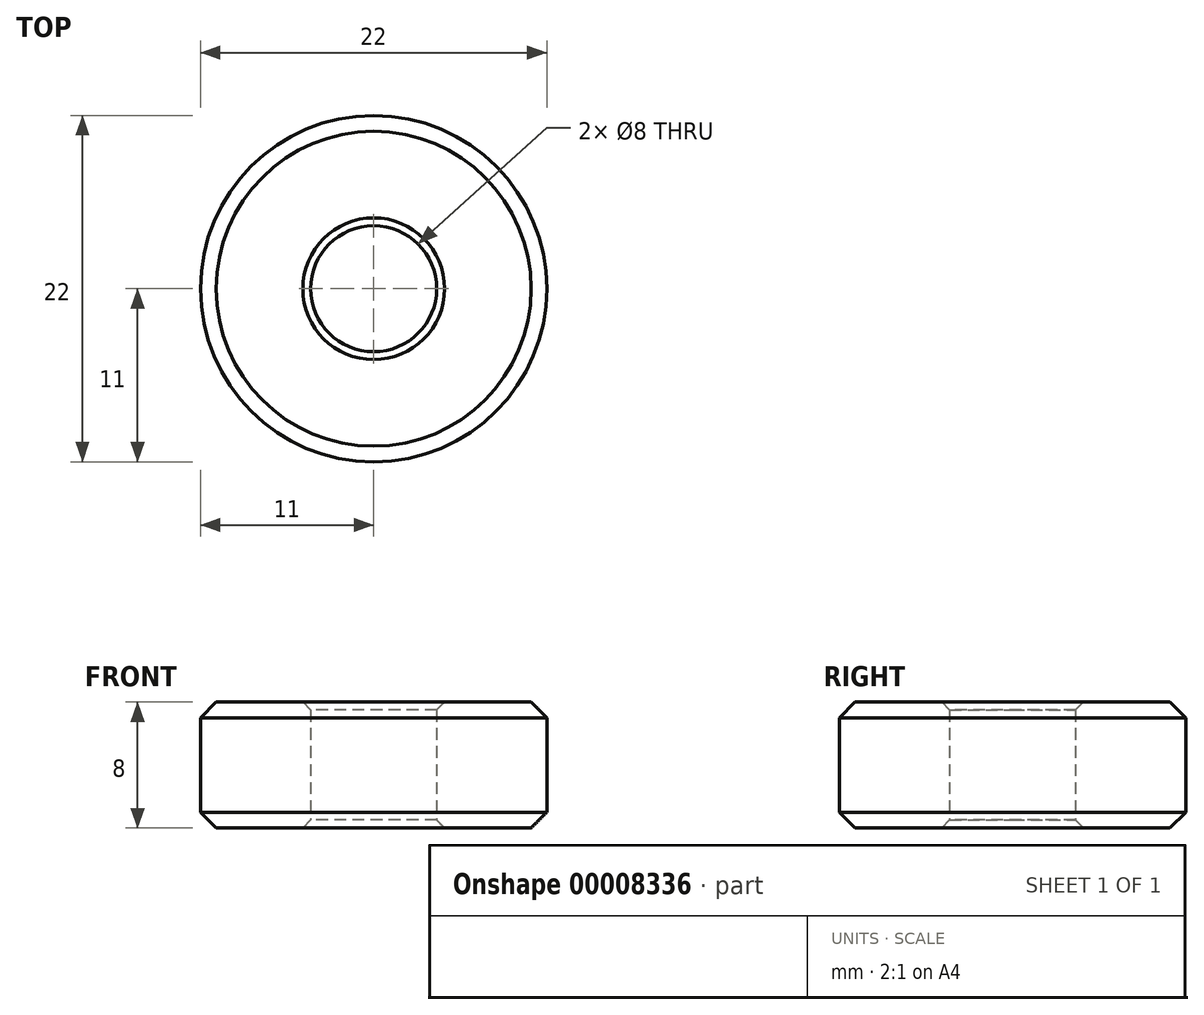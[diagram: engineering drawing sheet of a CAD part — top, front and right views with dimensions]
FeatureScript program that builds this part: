
annotation { "Feature Type Name" : "Feature", "Feature Type Description" : "" }
export const myFeature = defineFeature(function(context is Context, id is Id, definition is map)
    precondition{}
    {
        {
            var Q0;
            Q0=qCreatedBy(makeId("Top.planeOp"),FACE);
            var sketch = newSketch(context, id + "F0", { "sketchPlane" : qUnion([Q0])});
            skCircle(sketch, "E0", {"center": v(0, 0) * mm, "radius": 4 * mm});
            skCircle(sketch, "E1", {"center": v(0, 0) * mm, "radius": 11 * mm});
            skSolve(sketch);
        }
        {
            var Q0;
            Q0 = qSketchRegion(id + "F0", true);
            extrude(context, id + "F1", {"entities" : qUnion([Q0]), "depth" : 8 * mm});
        }
        {
            var Q0;
            Q0=makeQuery(id+"F1.opExtrude","CAP_EDGE",EDGE,{"disambiguationData":[OSD([sQuery(id+"F0.wireOp",EDGE,"E1")])],"isStart":false});
            var Q1;
            Q1=makeQuery(id+"F1.opExtrude","CAP_EDGE",EDGE,{"disambiguationData":[OSD([sQuery(id+"F0.wireOp",EDGE,"E1")])],"isStart":true});
            chamfer(context, id + "F2", {"entities" : qUnion([Q0, Q1]), "width" : 1 * mm, "tangentPropagation" : true});
        }
        {
            var Q0;
            Q0=makeQuery(id+"F1.opExtrude","CAP_EDGE",EDGE,{"disambiguationData":[OSD([sQuery(id+"F0.wireOp",EDGE,"E0")])],"isStart":false});
            var Q1;
            Q1=makeQuery(id+"F1.opExtrude","CAP_EDGE",EDGE,{"disambiguationData":[OSD([sQuery(id+"F0.wireOp",EDGE,"E0")])],"isStart":true});
            chamfer(context, id + "F3", {"entities" : qUnion([Q0, Q1]), "width" : 0.5 * mm, "tangentPropagation" : true});
        }
    });
